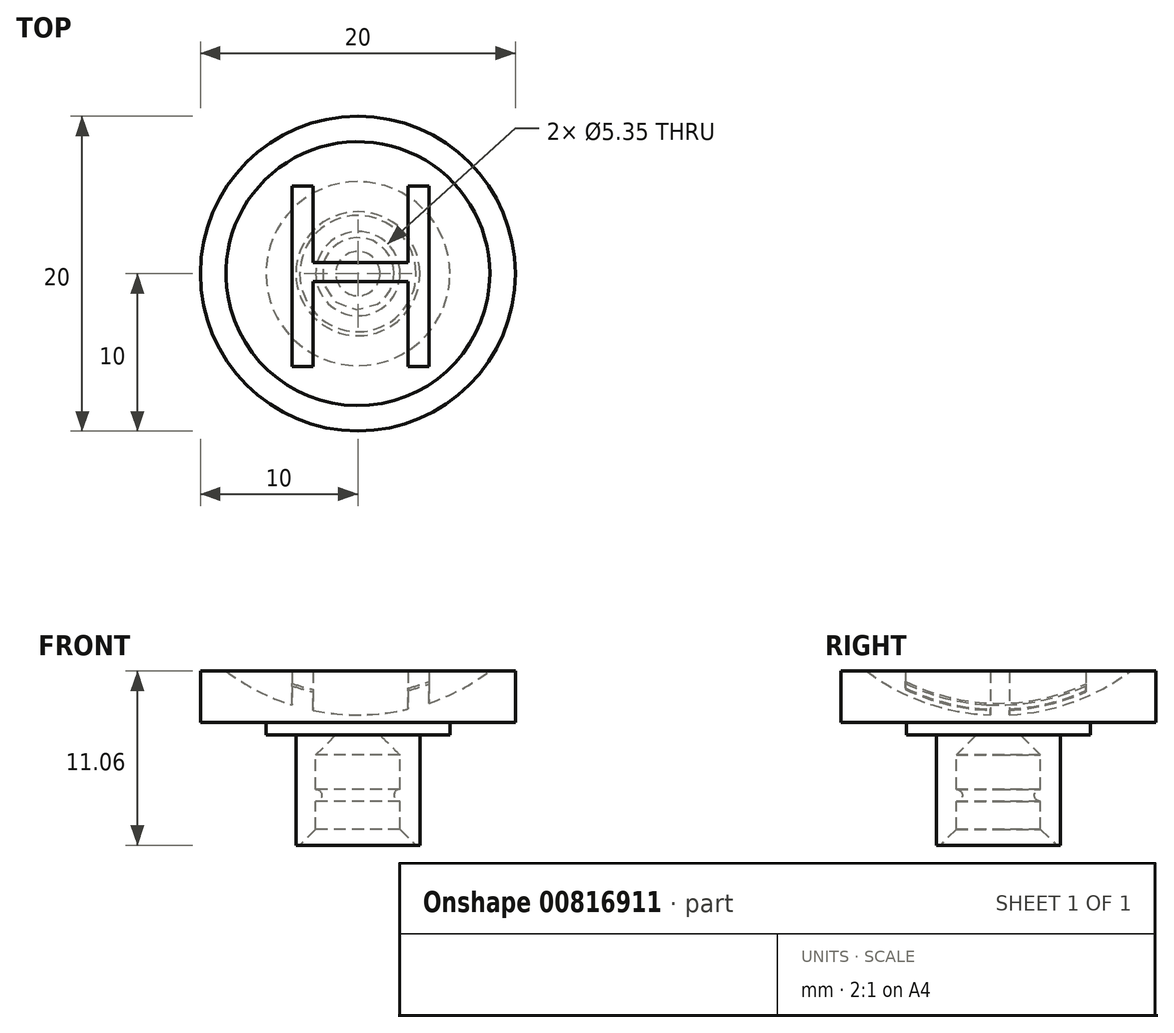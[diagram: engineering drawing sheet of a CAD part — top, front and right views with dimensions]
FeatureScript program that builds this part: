
annotation { "Feature Type Name" : "Feature", "Feature Type Description" : "" }
export const myFeature = defineFeature(function(context is Context, id is Id, definition is map)
    precondition{}
    {
        {
            var Q0;
            Q0=qCreatedBy(makeId("Front.planeOp"),FACE);
            var sketch = newSketch(context, id + "F0", { "sketchPlane" : qUnion([Q0])});
            skLineSegment(sketch, "E0", {"start": v(2.68, 0) * mm, "end": v(2.68, -3.44) * mm});
            skLineSegment(sketch, "E1", {"start": v(2.68, -7) * mm, "end": v(3.94, -7) * mm});
            skLineSegment(sketch, "E2", {"start": v(3.94, -7) * mm, "end": v(3.94, 0) * mm});
            skLineSegment(sketch, "E3", {"start": v(3.94, 0) * mm, "end": v(10, 0) * mm});
            skLineSegment(sketch, "E4", {"start": v(10, 0) * mm, "end": v(10, 5.48) * mm});
            skArc(sketch, "E5", {"start": v(0, 1.27) * mm, "mid": v(5.43, 2.37) * mm, "end": v(10, 5.48) * mm});
            skLineSegment(sketch, "E6", {"start": v(0, 1.27) * mm, "end": v(0, 0) * mm});
            skLineSegment(sketch, "E7", {"start": v(0, 0) * mm, "end": v(2.68, 0) * mm});
            skArc(sketch, "E8", {"start": v(2.68, -3.44) * mm, "mid": v(2.3, -3.82) * mm, "end": v(2.68, -4.2) * mm});
            skLineSegment(sketch, "E9.trimOffspring", {"start": v(2.68, -4.2) * mm, "end": v(2.68, -7) * mm});
            skSolve(sketch);
        }
        {
            var Q0;
            Q0 = qSketchRegion(id + "F0", true);
            var Q1;
            Q1=sQuery(id+"F0.wireOp",EDGE,"E6");
            revolve(context, id + "F1", {"surfaceOperationType" : NewSurfaceOperationType.NEW, "entities" : qUnion([Q0]), "axis" : qUnion([Q1]), "revolveType" : RevolveType.FULL});
        }
        {
            var Q0;
            Q0=qCreatedBy(makeId("Top.planeOp"),FACE);
            var sketch = newSketch(context, id + "F2", { "sketchPlane" : qUnion([Q0])});
            skText(sketch, "E10", { "text": "H", "fontName": "OpenSans-Regular.ttf"});
            const initialGuessF2  = {"E10": [-0.00575, -0.00589, 1, 0, 0.01156]};
            skSetInitialGuess(sketch, initialGuessF2);
            skSolve(sketch);
        }
        {
            var Q0;
            Q0 = qSketchRegion(id + "F2", true);
            extrude(context, id + "F3", {"entities" : qUnion([Q0]), "operationType" : NewBodyOperationType.ADD, "depth" : 4.06 * mm, "offsetDistance" : 25.4 * mm});
        }
        {
            var Q0;
            Q0=qCreatedBy(makeId("Right.planeOp"),FACE);
            var sketch = newSketch(context, id + "F4", { "sketchPlane" : qUnion([Q0])});
            skLineSegment(sketch, "E11.bottom", {"start": v(-17.16, 8.86) * mm, "end": v(19.43, 8.86) * mm});
            skLineSegment(sketch, "E11.top", {"start": v(-17.16, 4.06) * mm, "end": v(19.43, 4.06) * mm});
            skLineSegment(sketch, "E11.left", {"start": v(-17.16, 8.86) * mm, "end": v(-17.16, 4.06) * mm});
            skLineSegment(sketch, "E11.right", {"start": v(19.43, 8.86) * mm, "end": v(19.43, 4.06) * mm});
            skSolve(sketch);
        }
        {
            var Q0;
            Q0 = qSketchRegion(id + "F4", true);
            extrude(context, id + "F5", {"entities" : qUnion([Q0]), "operationType" : NewBodyOperationType.REMOVE, "endBound" : BoundingType.SYMMETRIC, "depth" : 25.4 * mm, "offsetDistance" : 25.4 * mm});
        }
        {
            var Q0;
            Q0=makeQuery(id+"F1.opRevolve","SWEPT_EDGE",EDGE,{"disambiguationData":[OSD([sQuery(id+"F0.wireOp",EDGE,"E0"),sQuery(id+"F0.wireOp",EDGE,"E7")])]});
            chamfer(context, id + "F6", {"entities" : qUnion([Q0]), "width" : 1.27 * mm, "tangentPropagation" : true});
        }
        {
            var Q0;
            Q0=makeQuery(id+"F1.opRevolve","SWEPT_FACE",FACE,{"disambiguationData":[OSD([sQuery(id+"F0.wireOp",EDGE,"E3")])]});
            var sketch = newSketch(context, id + "F7", { "sketchPlane" : qUnion([Q0])});
            skCircle(sketch, "E12", {"center": v(0, 0) * mm, "radius": 5.84 * mm});
            skCircle(sketch, "E13", {"center": v(0, 0) * mm, "radius": 14.72 * mm});
            skSolve(sketch);
        }
        {
            var Q0;
            Q0 = qSketchRegion(id + "F7", true);
            extrude(context, id + "F8", {"entities" : qUnion([Q0]), "operationType" : NewBodyOperationType.REMOVE, "oppositeDirection" : true, "depth" : .8 * mm, "offsetDistance" : 25.4 * mm});
        }
        {
            var Q0;
            Q0=makeQuery(id+"F1.opRevolve","SWEPT_EDGE",EDGE,{"disambiguationData":[OSD([sQuery(id+"F0.wireOp",EDGE,"E1"),sQuery(id+"F0.wireOp",EDGE,"E9.trimOffspring")])]});
            chamfer(context, id + "F9", {"entities" : qUnion([Q0]), "width" : 1.02 * mm, "tangentPropagation" : true});
        }
    });
